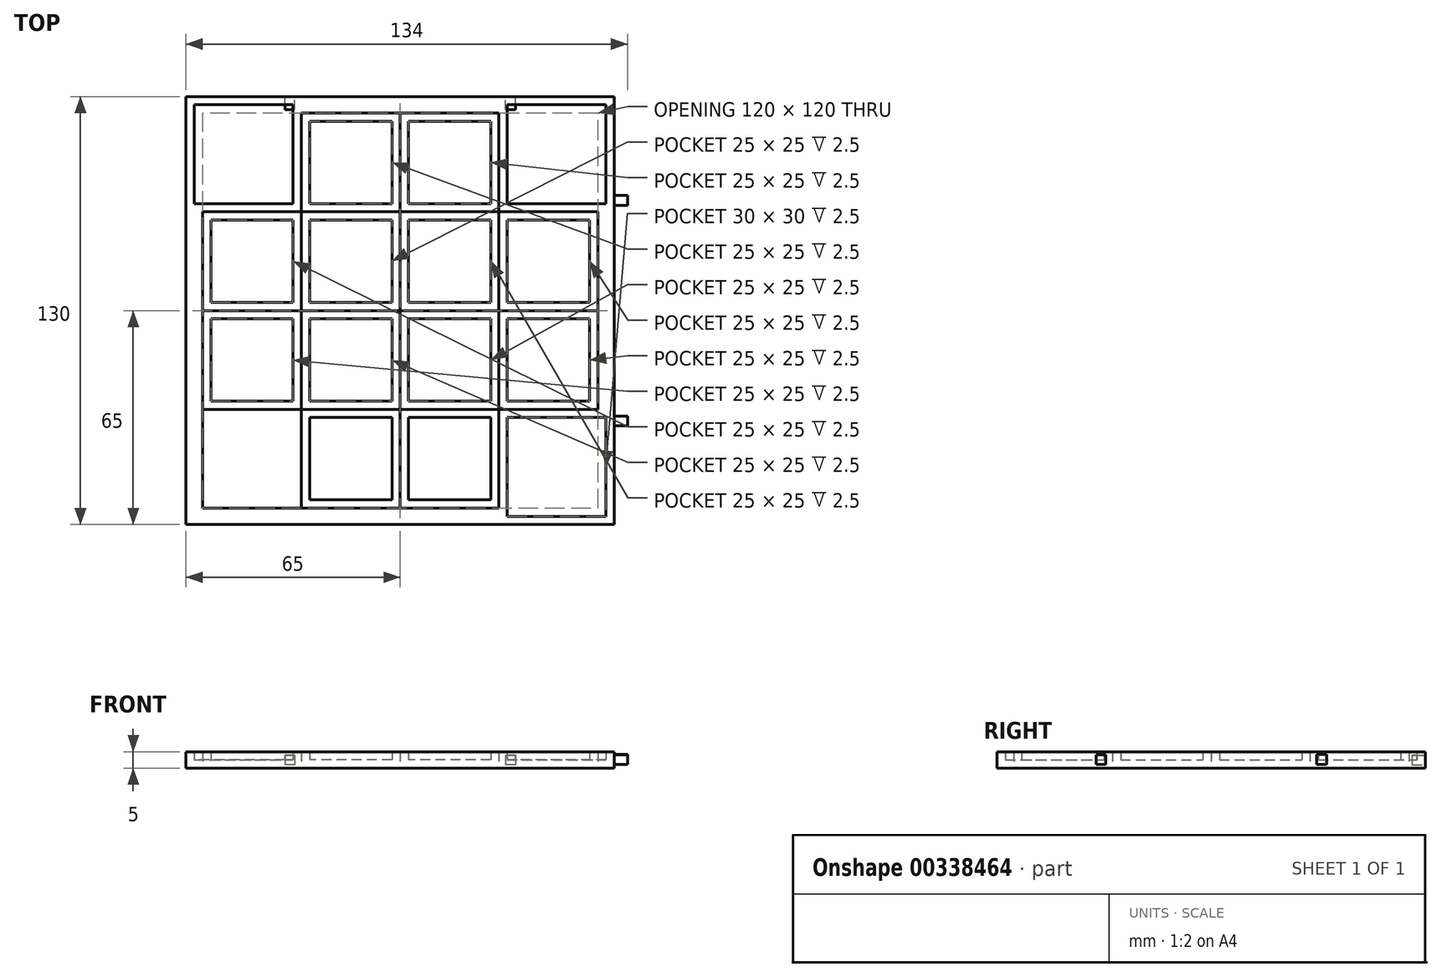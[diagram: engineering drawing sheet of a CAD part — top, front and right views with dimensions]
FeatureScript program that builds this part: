
annotation { "Feature Type Name" : "Feature", "Feature Type Description" : "" }
export const myFeature = defineFeature(function(context is Context, id is Id, definition is map)
    precondition{}
    {
        {
            var Q0;
            Q0=qCreatedBy(makeId("Top.planeOp"),FACE);
            var sketch = newSketch(context, id + "F0", { "sketchPlane" : qUnion([Q0])});
            skLineSegment(sketch, "E0.bottom", {"start": v(60, -60) * mm, "end": v(-60, -60) * mm});
            skLineSegment(sketch, "E0.top", {"start": v(60, 60) * mm, "end": v(-60, 60) * mm});
            skLineSegment(sketch, "E0.left", {"start": v(60, -60) * mm, "end": v(60, 60) * mm});
            skLineSegment(sketch, "E0.right", {"start": v(-60, -60) * mm, "end": v(-60, 60) * mm});
            skPoint(sketch, "E0.middle", {"position": v(0, 0) * mm});
            skLineSegment(sketch, "E1.bottom", {"start": v(-60, -60) * mm, "end": v(-30, -60) * mm});
            skLineSegment(sketch, "E1.top", {"start": v(-60, -30) * mm, "end": v(-30, -30) * mm});
            skLineSegment(sketch, "E1.left", {"start": v(-60, -60) * mm, "end": v(-60, -30) * mm});
            skLineSegment(sketch, "E1.right", {"start": v(-30, -60) * mm, "end": v(-30, -30) * mm});
            skLineSegment(sketch, "E2.0.1.0", {"start": v(-30, -30) * mm, "end": v(-30, 0) * mm});
            skLineSegment(sketch, "E2.0.1.1", {"start": v(-60, 0) * mm, "end": v(-30, 0) * mm});
            skLineSegment(sketch, "E2.0.2.0", {"start": v(-30, 0) * mm, "end": v(-30, 30) * mm});
            skLineSegment(sketch, "E2.0.2.1", {"start": v(-60, 30) * mm, "end": v(-30, 30) * mm});
            skLineSegment(sketch, "E2.0.3.0", {"start": v(-30, 30) * mm, "end": v(-30, 60) * mm});
            skLineSegment(sketch, "E2.0.3.1", {"start": v(-60, 60) * mm, "end": v(-30, 60) * mm});
            skLineSegment(sketch, "E2.1.0.0", {"start": v(0, -60) * mm, "end": v(0, -30) * mm});
            skLineSegment(sketch, "E2.1.0.1", {"start": v(-30, -30) * mm, "end": v(0, -30) * mm});
            skLineSegment(sketch, "E2.1.1.0", {"start": v(0, -30) * mm, "end": v(0, 0) * mm});
            skLineSegment(sketch, "E2.1.1.1", {"start": v(-30, 0) * mm, "end": v(0, 0) * mm});
            skLineSegment(sketch, "E2.1.2.0", {"start": v(0, 0) * mm, "end": v(0, 30) * mm});
            skLineSegment(sketch, "E2.1.2.1", {"start": v(-30, 30) * mm, "end": v(0, 30) * mm});
            skLineSegment(sketch, "E2.1.3.0", {"start": v(0, 30) * mm, "end": v(0, 60) * mm});
            skLineSegment(sketch, "E2.1.3.1", {"start": v(-30, 60) * mm, "end": v(0, 60) * mm});
            skLineSegment(sketch, "E2.2.0.0", {"start": v(30, -60) * mm, "end": v(30, -30) * mm});
            skLineSegment(sketch, "E2.2.0.1", {"start": v(0, -30) * mm, "end": v(30, -30) * mm});
            skLineSegment(sketch, "E2.2.1.0", {"start": v(30, -30) * mm, "end": v(30, 0) * mm});
            skLineSegment(sketch, "E2.2.1.1", {"start": v(0, 0) * mm, "end": v(30, 0) * mm});
            skLineSegment(sketch, "E2.2.2.0", {"start": v(30, 0) * mm, "end": v(30, 30) * mm});
            skLineSegment(sketch, "E2.2.2.1", {"start": v(0, 30) * mm, "end": v(30, 30) * mm});
            skLineSegment(sketch, "E2.2.3.0", {"start": v(30, 30) * mm, "end": v(30, 60) * mm});
            skLineSegment(sketch, "E2.2.3.1", {"start": v(0, 60) * mm, "end": v(30, 60) * mm});
            skLineSegment(sketch, "E2.3.0.0", {"start": v(60, -60) * mm, "end": v(60, -30) * mm});
            skLineSegment(sketch, "E2.3.0.1", {"start": v(30, -30) * mm, "end": v(60, -30) * mm});
            skLineSegment(sketch, "E2.3.1.0", {"start": v(60, -30) * mm, "end": v(60, 0) * mm});
            skLineSegment(sketch, "E2.3.1.1", {"start": v(30, 0) * mm, "end": v(60, 0) * mm});
            skLineSegment(sketch, "E2.3.2.0", {"start": v(60, 0) * mm, "end": v(60, 30) * mm});
            skLineSegment(sketch, "E2.3.2.1", {"start": v(30, 30) * mm, "end": v(60, 30) * mm});
            skLineSegment(sketch, "E2.3.3.0", {"start": v(60, 30) * mm, "end": v(60, 60) * mm});
            skLineSegment(sketch, "E2.3.3.1", {"start": v(30, 60) * mm, "end": v(60, 60) * mm});
            skLineSegment(sketch, "E2.direction1", {"start": v(-60, -30) * mm, "end": v(-30, -30) * mm, "construction": true});
            skLineSegment(sketch, "E2.direction2", {"start": v(-60, -30) * mm, "end": v(-60, 0) * mm, "construction": true});
            skLineSegment(sketch, "E3.bottom", {"start": v(65, -65) * mm, "end": v(-65, -65) * mm});
            skLineSegment(sketch, "E3.top", {"start": v(65, 65) * mm, "end": v(-65, 65) * mm});
            skLineSegment(sketch, "E3.left", {"start": v(65, -65) * mm, "end": v(65, 65) * mm});
            skLineSegment(sketch, "E3.right", {"start": v(-65, -65) * mm, "end": v(-65, 65) * mm});
            skSolve(sketch);
        }
        {
            var Q0;
            Q0 = qSketchRegion(id + "F0", true);
            extrude(context, id + "F1", {"entities" : qUnion([Q0]), "depth" : 5 * mm});
        }
        {
            var Q0;
            {var subQ2=sQuery(id+"F0.wireOp",EDGE,"E2.2.0.0");Q0=makeQuery(id+"F0.imprint","IMPRINT",FACE,{"disambiguationData":[TD([[makeQuery(id+"F0.imprint","IMPRINT",EDGE,{"derivedFrom":subQ2}),-1.0]])]});}
            var Q1;
            Q1=makeQuery(id+"F0.imprint","IMPRINT",FACE,{"disambiguationData":[TD([[makeQuery(id+"F0.imprint","IMPRINT",EDGE,{"derivedFrom":sQuery(id+"F0.wireOp",EDGE,"E2.1.1.0")}),-1.0]])]});
            var Q2;
            Q2=makeQuery(id+"F0.imprint","IMPRINT",FACE,{"disambiguationData":[TD([[makeQuery(id+"F0.imprint","IMPRINT",EDGE,{"derivedFrom":sQuery(id+"F0.wireOp",EDGE,"E2.0.2.0")}),-1.0]])]});
            var Q3;
            {var subQ2=sQuery(id+"F0.wireOp",EDGE,"E2.0.2.1");Q3=makeQuery(id+"F0.imprint","IMPRINT",FACE,{"disambiguationData":[TD([[makeQuery(id+"F0.imprint","IMPRINT",EDGE,{"derivedFrom":subQ2}),1.0]])]});}
            var Q4;
            Q4=makeQuery(id+"F0.imprint","IMPRINT",FACE,{"disambiguationData":[TD([[makeQuery(id+"F0.imprint","IMPRINT",EDGE,{"derivedFrom":sQuery(id+"F0.wireOp",EDGE,"E1.bottom")}),1.0]])]});
            var Q5;
            Q5=makeQuery(id+"F0.imprint","IMPRINT",FACE,{"disambiguationData":[TD([[makeQuery(id+"F0.imprint","IMPRINT",EDGE,{"derivedFrom":sQuery(id+"F0.wireOp",EDGE,"E2.2.3.0")}),-1.0]])]});
            extrude(context, id + "F2", {"entities" : qUnion([Q0, Q1, Q2, Q3, Q4, Q5]), "operationType" : NewBodyOperationType.ADD, "depth" : 5 * mm});
        }
        {
            var Q0;
            Q0=makeQuery(id+"F2.opExtrude","CAP_FACE",FACE,{"disambiguationData":[OSD([sQuery(id+"F0.wireOp",EDGE,"E2.1.1.0"),sQuery(id+"F0.wireOp",EDGE,"E2.2.0.1"),sQuery(id+"F0.wireOp",EDGE,"E2.2.1.0"),sQuery(id+"F0.wireOp",EDGE,"E2.2.1.1")])],"isStart":false});
            var Q1;
            Q1=makeQuery(id+"F2.opExtrude","CAP_FACE",FACE,{"disambiguationData":[OSD([sQuery(id+"F0.wireOp",EDGE,"E2.0.2.0"),sQuery(id+"F0.wireOp",EDGE,"E2.1.1.1"),sQuery(id+"F0.wireOp",EDGE,"E2.1.2.0"),sQuery(id+"F0.wireOp",EDGE,"E2.1.2.1")])],"isStart":false});
            var Q2;
            Q2=makeQuery(id+"F2.opExtrude","CAP_FACE",FACE,{"disambiguationData":[OSD([sQuery(id+"F0.wireOp",EDGE,"E1.bottom"),sQuery(id+"F0.wireOp",EDGE,"E1.top"),sQuery(id+"F0.wireOp",EDGE,"E1.left"),sQuery(id+"F0.wireOp",EDGE,"E1.right")])],"isStart":false});
            var Q3;
            Q3=makeQuery(id+"F2.opExtrude","CAP_FACE",FACE,{"disambiguationData":[OSD([sQuery(id+"F0.wireOp",EDGE,"E0.bottom"),sQuery(id+"F0.wireOp",EDGE,"E2.2.0.0"),sQuery(id+"F0.wireOp",EDGE,"E2.3.0.0"),sQuery(id+"F0.wireOp",EDGE,"E2.3.0.1")])],"isStart":false});
            var Q4;
            Q4=makeQuery(id+"F2.opExtrude","CAP_FACE",FACE,{"disambiguationData":[OSD([sQuery(id+"F0.wireOp",EDGE,"E0.right"),sQuery(id+"F0.wireOp",EDGE,"E2.0.2.1"),sQuery(id+"F0.wireOp",EDGE,"E2.0.3.0"),sQuery(id+"F0.wireOp",EDGE,"E2.0.3.1")])],"isStart":false});
            var Q5;
            Q5=makeQuery(id+"F2.opExtrude","CAP_FACE",FACE,{"disambiguationData":[OSD([sQuery(id+"F0.wireOp",EDGE,"E2.2.3.0"),sQuery(id+"F0.wireOp",EDGE,"E2.3.2.1"),sQuery(id+"F0.wireOp",EDGE,"E2.3.3.0"),sQuery(id+"F0.wireOp",EDGE,"E2.3.3.1")])],"isStart":false});
            shell(context, id + "F3", {"entities" : qUnion([Q0, Q1, Q2, Q3, Q4, Q5]), "thickness" : 2.5 * mm});
        }
        {
            var Q0;
            Q0=makeQuery(id+"F0.imprint","IMPRINT",FACE,{"disambiguationData":[TD([[makeQuery(id+"F0.imprint","IMPRINT",EDGE,{"derivedFrom":sQuery(id+"F0.wireOp",EDGE,"E2.0.1.0")}),-1.0]])]});
            var Q1;
            Q1=makeQuery(id+"F0.imprint","IMPRINT",FACE,{"disambiguationData":[TD([[makeQuery(id+"F0.imprint","IMPRINT",EDGE,{"derivedFrom":sQuery(id+"F0.wireOp",EDGE,"E2.1.2.0")}),-1.0]])]});
            var Q2;
            {var subQ0=sQuery(id+"F0.wireOp",EDGE,"E2.0.1.1");Q2=makeQuery(id+"F0.imprint","IMPRINT",FACE,{"disambiguationData":[TD([[makeQuery(id+"F0.imprint","IMPRINT",EDGE,{"derivedFrom":subQ0}),1.0]])]});}
            var Q3;
            Q3=makeQuery(id+"F0.imprint","IMPRINT",FACE,{"disambiguationData":[TD([[makeQuery(id+"F0.imprint","IMPRINT",EDGE,{"derivedFrom":sQuery(id+"F0.wireOp",EDGE,"E2.0.3.0")}),-1.0]])]});
            var Q4;
            {var subQ0=sQuery(id+"F0.wireOp",EDGE,"E2.1.0.0");Q4=makeQuery(id+"F0.imprint","IMPRINT",FACE,{"disambiguationData":[TD([[makeQuery(id+"F0.imprint","IMPRINT",EDGE,{"derivedFrom":subQ0}),-1.0]])]});}
            var Q5;
            Q5=makeQuery(id+"F0.imprint","IMPRINT",FACE,{"disambiguationData":[TD([[makeQuery(id+"F0.imprint","IMPRINT",EDGE,{"derivedFrom":sQuery(id+"F0.wireOp",EDGE,"E2.2.1.0")}),-1.0]])]});
            extrude(context, id + "F4", {"entities" : qUnion([Q0, Q1, Q2, Q3, Q4, Q5]), "depth" : 5 * mm});
        }
        {
            var Q0;
            Q0=makeQuery(id+"F4.opExtrude","CAP_FACE",FACE,{"disambiguationData":[OSD([sQuery(id+"F0.wireOp",EDGE,"E0.right"),sQuery(id+"F0.wireOp",EDGE,"E2.0.1.1"),sQuery(id+"F0.wireOp",EDGE,"E2.0.2.0"),sQuery(id+"F0.wireOp",EDGE,"E2.0.2.1")])],"isStart":false});
            var Q1;
            Q1=makeQuery(id+"F4.opExtrude","CAP_FACE",FACE,{"disambiguationData":[OSD([sQuery(id+"F0.wireOp",EDGE,"E2.0.3.0"),sQuery(id+"F0.wireOp",EDGE,"E2.1.2.1"),sQuery(id+"F0.wireOp",EDGE,"E2.1.3.0"),sQuery(id+"F0.wireOp",EDGE,"E2.1.3.1")])],"isStart":false});
            var Q2;
            Q2=makeQuery(id+"F4.opExtrude","CAP_FACE",FACE,{"disambiguationData":[OSD([sQuery(id+"F0.wireOp",EDGE,"E2.1.2.0"),sQuery(id+"F0.wireOp",EDGE,"E2.2.1.1"),sQuery(id+"F0.wireOp",EDGE,"E2.2.2.0"),sQuery(id+"F0.wireOp",EDGE,"E2.2.2.1")])],"isStart":false});
            var Q3;
            Q3=makeQuery(id+"F4.opExtrude","CAP_FACE",FACE,{"disambiguationData":[OSD([sQuery(id+"F0.wireOp",EDGE,"E2.0.1.0"),sQuery(id+"F0.wireOp",EDGE,"E2.1.0.1"),sQuery(id+"F0.wireOp",EDGE,"E2.1.1.0"),sQuery(id+"F0.wireOp",EDGE,"E2.1.1.1")])],"isStart":false});
            var Q4;
            Q4=makeQuery(id+"F4.opExtrude","CAP_FACE",FACE,{"disambiguationData":[OSD([sQuery(id+"F0.wireOp",EDGE,"E2.2.1.0"),sQuery(id+"F0.wireOp",EDGE,"E2.3.0.1"),sQuery(id+"F0.wireOp",EDGE,"E2.3.1.0"),sQuery(id+"F0.wireOp",EDGE,"E2.3.1.1")])],"isStart":false});
            var Q5;
            Q5=makeQuery(id+"F4.opExtrude","CAP_FACE",FACE,{"disambiguationData":[OSD([sQuery(id+"F0.wireOp",EDGE,"E0.bottom"),sQuery(id+"F0.wireOp",EDGE,"E2.1.0.0"),sQuery(id+"F0.wireOp",EDGE,"E2.2.0.0"),sQuery(id+"F0.wireOp",EDGE,"E2.2.0.1")])],"isStart":false});
            shell(context, id + "F5", {"entities" : qUnion([Q0, Q1, Q2, Q3, Q4, Q5]), "thickness" : 2.5 * mm});
        }
        {
            var Q0;
            {var subQ0=sQuery(id+"F0.wireOp",EDGE,"E1.top");Q0=makeQuery(id+"F0.imprint","IMPRINT",FACE,{"disambiguationData":[TD([[makeQuery(id+"F0.imprint","IMPRINT",EDGE,{"derivedFrom":subQ0}),1.0]])]});}
            var Q1;
            Q1=makeQuery(id+"F0.imprint","IMPRINT",FACE,{"disambiguationData":[TD([[makeQuery(id+"F0.imprint","IMPRINT",EDGE,{"derivedFrom":sQuery(id+"F0.wireOp",EDGE,"E2.2.2.0")}),-1.0]])]});
            var Q2;
            Q2=makeQuery(id+"F0.imprint","IMPRINT",FACE,{"disambiguationData":[TD([[makeQuery(id+"F0.imprint","IMPRINT",EDGE,{"derivedFrom":sQuery(id+"F0.wireOp",EDGE,"E2.1.3.0")}),-1.0]])]});
            var Q3;
            {var subQ0=sQuery(id+"F0.wireOp",EDGE,"E1.right");Q3=makeQuery(id+"F0.imprint","IMPRINT",FACE,{"disambiguationData":[TD([[makeQuery(id+"F0.imprint","IMPRINT",EDGE,{"derivedFrom":subQ0}),-1.0]])]});}
            var Q4;
            {var subQ0=sQuery(id+"F0.wireOp",EDGE,"E1.top");Q4=makeQuery(id+"F0.imprint","IMPRINT",FACE,{"disambiguationData":[TD([[makeQuery(id+"F0.imprint","IMPRINT",EDGE,{"derivedFrom":subQ0}),1.0]])]});}
            var Q5;
            {var subQ0=sQuery(id+"F0.wireOp",EDGE,"E1.right");Q5=makeQuery(id+"F0.imprint","IMPRINT",FACE,{"disambiguationData":[TD([[makeQuery(id+"F0.imprint","IMPRINT",EDGE,{"derivedFrom":subQ0}),-1.0]])]});}
            extrude(context, id + "F6", {"entities" : qUnion([Q0, Q1, Q2, Q3, Q4, Q5]), "depth" : 5 * mm});
        }
        {
            var Q0;
            Q0=makeQuery(id+"F6.opExtrude","CAP_FACE",FACE,{"disambiguationData":[OSD([sQuery(id+"F0.wireOp",EDGE,"E0.right"),sQuery(id+"F0.wireOp",EDGE,"E1.top"),sQuery(id+"F0.wireOp",EDGE,"E2.0.1.0"),sQuery(id+"F0.wireOp",EDGE,"E2.0.1.1")])],"isStart":false});
            var Q1;
            Q1=makeQuery(id+"F6.opExtrude","CAP_FACE",FACE,{"disambiguationData":[OSD([sQuery(id+"F0.wireOp",EDGE,"E2.2.2.0"),sQuery(id+"F0.wireOp",EDGE,"E2.3.1.1"),sQuery(id+"F0.wireOp",EDGE,"E2.3.2.0"),sQuery(id+"F0.wireOp",EDGE,"E2.3.2.1")])],"isStart":false});
            var Q2;
            Q2=makeQuery(id+"F6.opExtrude","CAP_FACE",FACE,{"disambiguationData":[OSD([sQuery(id+"F0.wireOp",EDGE,"E2.1.3.0"),sQuery(id+"F0.wireOp",EDGE,"E2.2.2.1"),sQuery(id+"F0.wireOp",EDGE,"E2.2.3.0"),sQuery(id+"F0.wireOp",EDGE,"E2.2.3.1")])],"isStart":false});
            var Q3;
            Q3=makeQuery(id+"F6.opExtrude","CAP_FACE",FACE,{"disambiguationData":[OSD([sQuery(id+"F0.wireOp",EDGE,"E0.bottom"),sQuery(id+"F0.wireOp",EDGE,"E1.right"),sQuery(id+"F0.wireOp",EDGE,"E2.1.0.0"),sQuery(id+"F0.wireOp",EDGE,"E2.1.0.1")])],"isStart":false});
            shell(context, id + "F7", {"entities" : qUnion([Q0, Q1, Q2, Q3]), "thickness" : 2.5 * mm});
        }
        {
            var Q0;
            Q0=makeQuery(id+"F1.opExtrude","SWEPT_FACE",FACE,{"disambiguationData":[OSD([sQuery(id+"F0.wireOp",EDGE,"E3.left")])]});
            var sketch = newSketch(context, id + "F8", { "sketchPlane" : qUnion([Q0])});
            skLineSegment(sketch, "E4.bottom", {"start": v(-65, 5) * mm, "end": v(65, 5) * mm});
            skLineSegment(sketch, "E4.top", {"start": v(-65, 0) * mm, "end": v(65, 0) * mm});
            skLineSegment(sketch, "E4.left", {"start": v(-65, 5) * mm, "end": v(-65, 0) * mm});
            skLineSegment(sketch, "E4.right", {"start": v(65, 5) * mm, "end": v(65, 0) * mm});
            skLineSegment(sketch, "E5.bottom", {"start": v(-35, 4.11) * mm, "end": v(-32, 4.11) * mm});
            skLineSegment(sketch, "E5.top", {"start": v(-35, 1.11) * mm, "end": v(-32, 1.11) * mm});
            skLineSegment(sketch, "E5.left", {"start": v(-35, 4.11) * mm, "end": v(-35, 1.11) * mm});
            skLineSegment(sketch, "E5.right", {"start": v(-32, 4.11) * mm, "end": v(-32, 1.11) * mm});
            skLineSegment(sketch, "E6.bottom", {"start": v(32, 4.15) * mm, "end": v(35, 4.15) * mm});
            skLineSegment(sketch, "E6.top", {"start": v(32, 1.15) * mm, "end": v(35, 1.15) * mm});
            skLineSegment(sketch, "E6.left", {"start": v(32, 4.15) * mm, "end": v(32, 1.15) * mm});
            skLineSegment(sketch, "E6.right", {"start": v(35, 4.15) * mm, "end": v(35, 1.15) * mm});
            skSolve(sketch);
        }
        {
            var Q0;
            Q0=makeQuery(id+"F8.imprint","IMPRINT",FACE,{"disambiguationData":[TD([[makeQuery(id+"F8.imprint","IMPRINT",EDGE,{"derivedFrom":sQuery(id+"F8.wireOp",EDGE,"E5.bottom")}),-1.0]])]});
            var Q1;
            Q1=makeQuery(id+"F8.imprint","IMPRINT",FACE,{"disambiguationData":[TD([[makeQuery(id+"F8.imprint","IMPRINT",EDGE,{"derivedFrom":sQuery(id+"F8.wireOp",EDGE,"E6.bottom")}),-1.0]])]});
            extrude(context, id + "F9", {"entities" : qUnion([Q0, Q1]), "operationType" : NewBodyOperationType.ADD, "depth" : 4 * mm});
        }
        {
            var Q0;
            Q0=makeQuery(id+"F1.opExtrude","SWEPT_FACE",FACE,{"disambiguationData":[OSD([sQuery(id+"F0.wireOp",EDGE,"E3.top")])]});
            var sketch = newSketch(context, id + "F10", { "sketchPlane" : qUnion([Q0])});
            skLineSegment(sketch, "E7.bottom", {"start": v(32, 4) * mm, "end": v(35, 4) * mm});
            skLineSegment(sketch, "E7.top", {"start": v(32, 1) * mm, "end": v(35, 1) * mm});
            skLineSegment(sketch, "E7.left", {"start": v(32, 4) * mm, "end": v(32, 1) * mm});
            skLineSegment(sketch, "E7.right", {"start": v(35, 4) * mm, "end": v(35, 1) * mm});
            skLineSegment(sketch, "E8.bottom", {"start": v(-35, 4) * mm, "end": v(-32, 4) * mm});
            skLineSegment(sketch, "E8.top", {"start": v(-35, 1) * mm, "end": v(-32, 1) * mm});
            skLineSegment(sketch, "E8.left", {"start": v(-35, 4) * mm, "end": v(-35, 1) * mm});
            skLineSegment(sketch, "E8.right", {"start": v(-32, 4) * mm, "end": v(-32, 1) * mm});
            skSolve(sketch);
        }
        {
            var Q0;
            Q0=makeQuery(id+"F10.imprint","IMPRINT",FACE,{"disambiguationData":[TD([[makeQuery(id+"F10.imprint","IMPRINT",EDGE,{"derivedFrom":sQuery(id+"F10.wireOp",EDGE,"E7.bottom")}),-1.0]])]});
            var Q1;
            Q1=makeQuery(id+"F10.imprint","IMPRINT",FACE,{"disambiguationData":[TD([[makeQuery(id+"F10.imprint","IMPRINT",EDGE,{"derivedFrom":sQuery(id+"F10.wireOp",EDGE,"E8.bottom")}),-1.0]])]});
            extrude(context, id + "F11", {"entities" : qUnion([Q0, Q1]), "operationType" : NewBodyOperationType.REMOVE, "oppositeDirection" : true, "depth" : 4 * mm});
        }
    });
